# Revit family: SA 8H7W
name_source: partatom
category: Mechanical Equipment
units: mm (PartAtom-declared; Revit-internal decimal feet)

## family parameters
Always vertical = Yes
Cut with Voids When Loaded = No
OmniClass Number = 23.75.00.00
OmniClass Title = Climate Control (HVAC)
Part Type = Normal
Room Calculation Point = No
Round Connector Dimension = Use Diameter
Shared = No
Work Plane-Based = No

## types (6) — shared parameters
Description = Energy Recovery Ventilator
Height = 13' - 9 1/4"
Manufacturer = Renewaire LLC
URL = www.renewaire.com
Width = 5' - 4 1/2"

## per-type parameters (varying)
| type | 3W | 4W | 5W | 6W | 7W | 8W | Airflow Range (CFM) | Cores (L125-G5) | Housing | Length | Model | Weight (lbs.) |
| 8H8W SA | No | No | No | No | No | Yes | 16,000 - 70,000 | 64 | <By Category> | 21' - 8 1/2" | 8H8W SA | 6,587 |
| 8H7W SA | No | No | No | No | Yes | No | 14,000 - 61,600 | 56 | <By Category> | 19' - 0" | 8H7W SA | 5,822 |
| 8H6W SA | No | No | No | Yes | No | No | 12,000 - 52,800 | 48 | <By Category> | 16' - 3 3/8" | 8H6W SA | 5,058 |
| 8H5W SA | No | No | Yes | No | No | No | 10,000 - 44,000 | 40 | <By Category> | 13' - 6 7/8" | 8H5W SA | 4,294 |
| 8H4W SA | No | Yes | No | No | No | No | 8,000 - 35,200 | 32 | <By Category> | 10' - 10 1/4" | 8H3W SA | 3,529 |
| 8H3W SA | Yes | No | No | No | No | No | 6,000 - 26400 | 24 | Metal - RenewAire - Anodized - Gray Text | 8' - 1 3/4" | 8H3W SA | 2,765 |

## geometry (parser evidence)
native form markers: Sweep x2
no freeform markers — native parametric forms only
